# Revit family: LWC
name_source: partatom
category: Lighting Fixtures
revit_build: Autodesk Revit MEP 2012 (Build: 20110916_2132(x64)
units: mm (PartAtom-declared; Revit-internal decimal feet)

## types (2) — shared parameters
Apparent Load = 0 VA
Backbox = White
Color Filter = 16777215
Default Elevation = 4.00'
Description = LWC LED is a premium, 10 inch wide wraparound with injection molded glowing ends sonically welded to the attractive acrylic prismatic lens.
Dimming Lamp Color Temperature Shift = <None>
Driver = Fixed Output
Emit from Line Length = 1.00'
Glass = White Glass
Lamp = LED Lamp
Manufacturer = Columbia Lighting
Manufacturer Fax = (866)-898-1065
Model = LWC
Product Documentation Link = http://www.columbialighting.com
Product Page URL = http://www.columbialighting.com
Tilt Angle = -90.00°
URL = http://www.columbialighting.com
Voltage = 120 V

## per-type parameters (varying)
| type | Lumen Output | Nominal Watts | Photometric Web File | Row Length |
| LWC4-40HL-EU | Very High Lumen | 55 W | LWC4-40HL-EU.ies | 4.00' |
| LWC2-40LW-EU | Low Lumen | 23 W | LWC2-40LW-EU.ies | 2.00' |

## geometry (parser evidence)
native form markers: Sweep x4
no freeform markers — native parametric forms only
